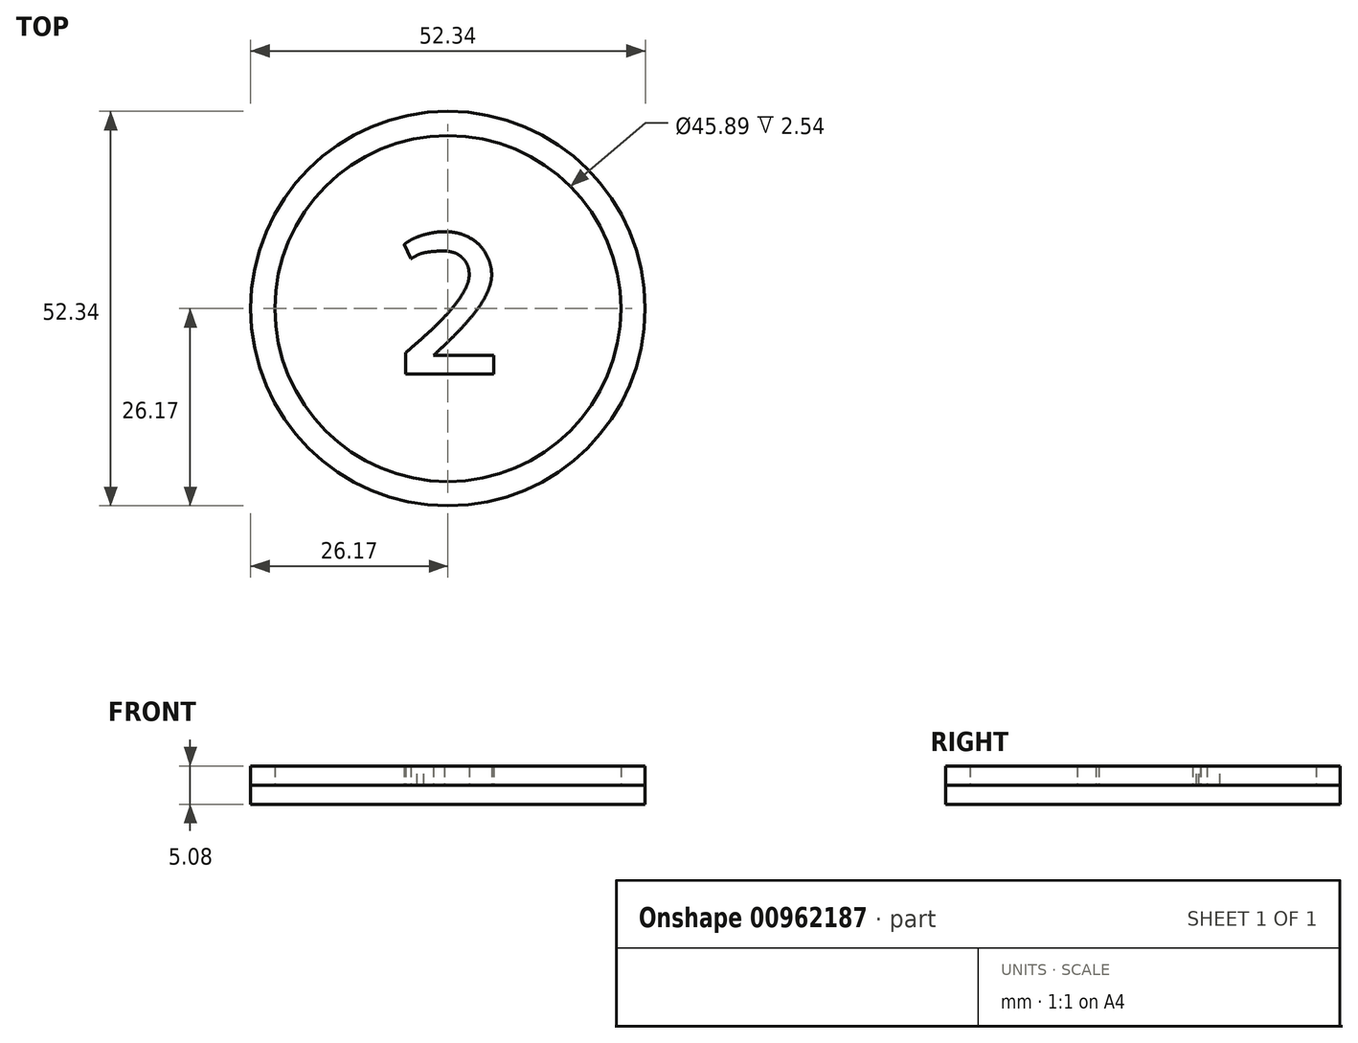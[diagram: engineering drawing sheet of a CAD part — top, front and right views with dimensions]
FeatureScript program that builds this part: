
annotation { "Feature Type Name" : "Feature", "Feature Type Description" : "" }
export const myFeature = defineFeature(function(context is Context, id is Id, definition is map)
    precondition{}
    {
        {
            var Q0;
            Q0=qCreatedBy(makeId("Top.planeOp"),FACE);
            var sketch = newSketch(context, id + "F0", { "sketchPlane" : qUnion([Q0])});
            skCircle(sketch, "E0", {"center": v(0, 0) * mm, "radius": 26.17 * mm});
            skCircle(sketch, "E1", {"center": v(0, 0) * mm, "radius": 22.94 * mm});
            skText(sketch, "E2", { "text": "2", "fontName": "AllertaStencil-Regular.ttf"});
            const initialGuessF0  = {"E2": [-0.00781, -0.0087, 1, 0, 0.01878]};
            skSetInitialGuess(sketch, initialGuessF0);
            skSolve(sketch);
        }
        {
            var Q0;
            Q0=makeQuery(id+"F0.imprint","IMPRINT",FACE,{"disambiguationData":[TD([[makeQuery(id+"F0.imprint","IMPRINT",EDGE,{"derivedFrom":sQuery(id+"F0.wireOp",EDGE,"E0")}),1.0]])]});
            var Q1;
            Q1=makeQuery(id+"F0.imprint","IMPRINT",FACE,{"disambiguationData":[TD([[makeQuery(id+"F0.imprint","IMPRINT",EDGE,{"derivedFrom":sQuery(id+"F0.wireOp",EDGE,"E2.sketch_text.stroke-0")}),-1.0]])]});
            extrude(context, id + "F1", {"entities" : qUnion([Q0, Q1]), "depth" : 2.54 * mm, "offsetDistance" : 25.4 * mm});
        }
        {
            var Q0;
            Q0=makeQuery(id+"F1.opExtrude","CAP_FACE",FACE,{"disambiguationData":[OSD([sQuery(id+"F0.wireOp",EDGE,"E0"),sQuery(id+"F0.wireOp",EDGE,"E1")])],"isStart":true});
            var sketch = newSketch(context, id + "F2", { "sketchPlane" : qUnion([Q0])});
            skCircle(sketch, "E3", {"center": v(0, 0) * mm, "radius": 26.17 * mm});
            skSolve(sketch);
        }
        {
            var Q0;
            Q0=qSketchRegion(id+"F2",true);
            extrude(context, id + "F3", {"entities" : qUnion([Q0]), "depth" : 2.54 * mm, "offsetDistance" : 25.4 * mm});
        }
    });
